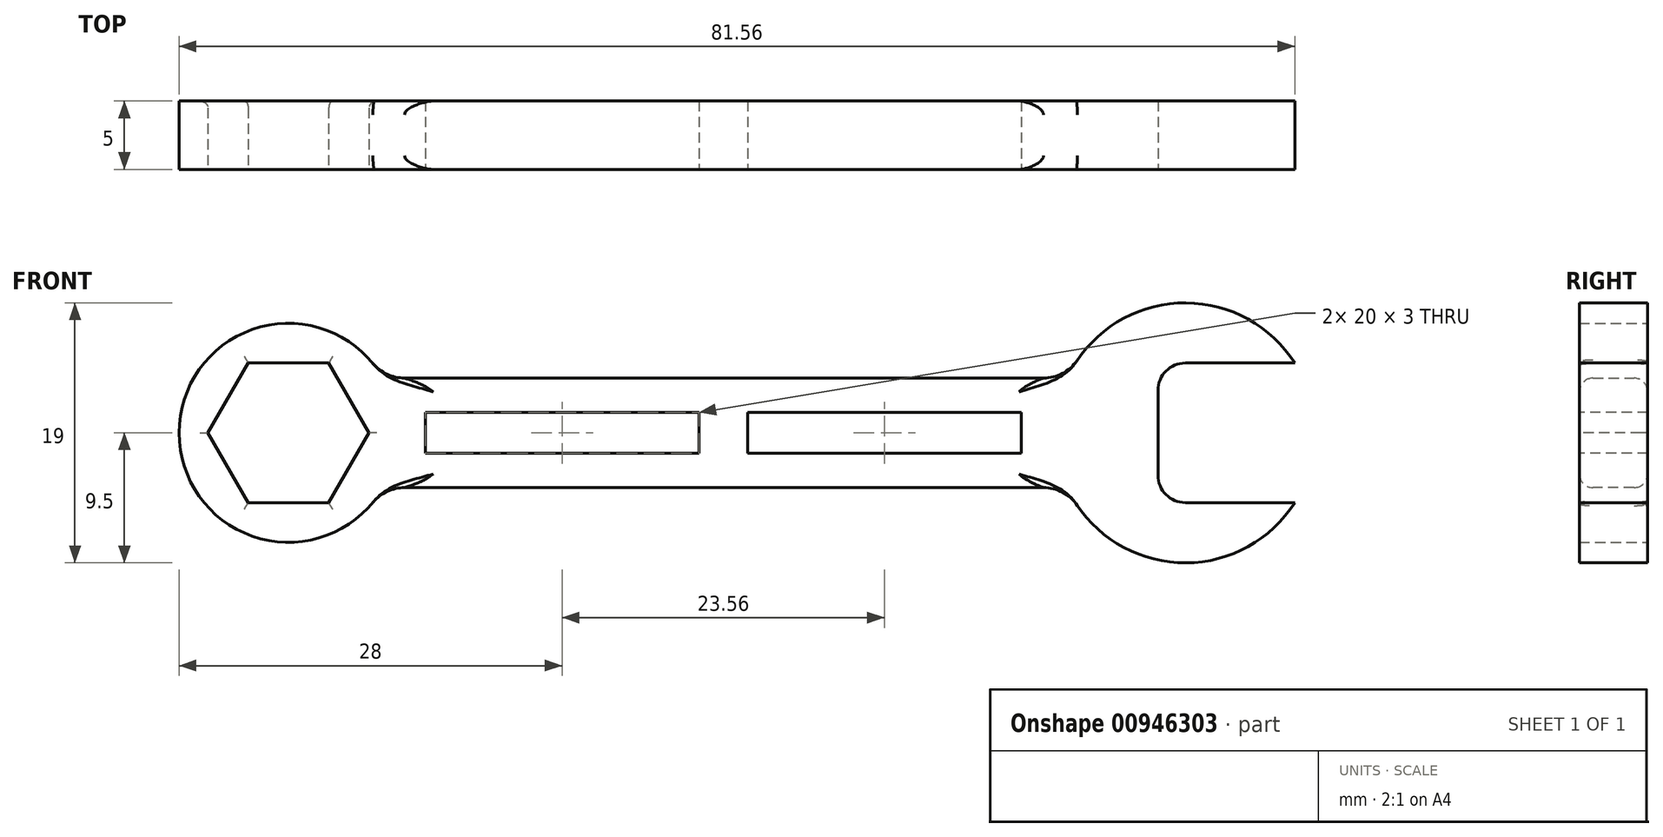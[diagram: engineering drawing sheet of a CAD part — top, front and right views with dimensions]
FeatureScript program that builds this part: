
annotation { "Feature Type Name" : "Feature", "Feature Type Description" : "" }
export const myFeature = defineFeature(function(context is Context, id is Id, definition is map)
    precondition{}
    {
        {
            var Q0;
            Q0=qCreatedBy(makeId("Front.planeOp"),FACE);
            var sketch = newSketch(context, id + "F0", { "sketchPlane" : qUnion([Q0])});
            skCircle(sketch, "E0", {"center": v(0, 0) * mm, "radius": 8 * mm});
            skLineSegment(sketch, "E1.bottom", {"start": v(6.93, 4) * mm, "end": v(56.93, 4) * mm});
            skLineSegment(sketch, "E1.top", {"start": v(6.93, -4) * mm, "end": v(56.93, -4) * mm});
            skLineSegment(sketch, "E1.left", {"start": v(6.93, 4) * mm, "end": v(6.93, -4) * mm});
            skLineSegment(sketch, "E1.right", {"start": v(56.93, 4) * mm, "end": v(56.93, -4) * mm});
            skCircle(sketch, "E2", {"center": v(65.55, 0) * mm, "radius": 9.5 * mm});
            skSolve(sketch);
        }
        {
            var Q0;
            {var subQ0=sQuery(id+"F0.wireOp",EDGE,"E1.left");Q0=makeQuery(id+"F0.imprint","IMPRINT",FACE,{"disambiguationData":[TD([[makeQuery(id+"F0.imprint","IMPRINT",EDGE,{"derivedFrom":subQ0}),-1.0]])]});}
            var Q1;
            {var subQ0=sQuery(id+"F0.wireOp",EDGE,"E1.left");Q1=makeQuery(id+"F0.imprint","IMPRINT",FACE,{"disambiguationData":[TD([[makeQuery(id+"F0.imprint","IMPRINT",EDGE,{"derivedFrom":subQ0}),1.0]])]});}
            var Q2;
            {var subQ1=sQuery(id+"F0.wireOp",EDGE,"E1.bottom");Q2=makeQuery(id+"F0.imprint","IMPRINT",FACE,{"disambiguationData":[TD([[makeQuery(id+"F0.imprint","IMPRINT",EDGE,{"derivedFrom":subQ1}),-1.0]])]});}
            var Q3;
            {var subQ0=sQuery(id+"F0.wireOp",EDGE,"E1.right");Q3=makeQuery(id+"F0.imprint","IMPRINT",FACE,{"disambiguationData":[TD([[makeQuery(id+"F0.imprint","IMPRINT",EDGE,{"derivedFrom":subQ0}),-1.0]])]});}
            var Q4;
            {var subQ0=sQuery(id+"F0.wireOp",EDGE,"E1.right");Q4=makeQuery(id+"F0.imprint","IMPRINT",FACE,{"disambiguationData":[TD([[makeQuery(id+"F0.imprint","IMPRINT",EDGE,{"derivedFrom":subQ0}),1.0]])]});}
            extrude(context, id + "F1", {"entities" : qUnion([Q0, Q1, Q2, Q3, Q4]), "depth" : 5 * mm, "offsetDistance" : 25 * mm});
        }
        {
            var Q0;
            Q0=makeQuery(id+"F1.opExtrude","CAP_FACE",FACE,{"disambiguationData":[OSD([sQuery(id+"F0.wireOp",EDGE,"E0"),sQuery(id+"F0.wireOp",EDGE,"E1.bottom"),sQuery(id+"F0.wireOp",EDGE,"E1.top"),sQuery(id+"F0.wireOp",EDGE,"E2")])],"isStart":false});
            var sketch = newSketch(context, id + "F2", { "sketchPlane" : qUnion([Q0])});
            skCircle(sketch, "E3.cCircle", {"center": v(0, 0) * mm, "radius": 5.1 * mm, "construction": true});
            skLineSegment(sketch, "E3.0", {"start": v(-2.94, 5.1) * mm, "end": v(2.94, 5.1) * mm});
            skLineSegment(sketch, "E3.1", {"start": v(2.94, 5.1) * mm, "end": v(5.89, 0) * mm});
            skLineSegment(sketch, "E3.2", {"start": v(5.89, 0) * mm, "end": v(2.94, -5.1) * mm});
            skLineSegment(sketch, "E3.3", {"start": v(2.94, -5.1) * mm, "end": v(-2.94, -5.1) * mm});
            skLineSegment(sketch, "E3.4", {"start": v(-2.94, -5.1) * mm, "end": v(-5.89, 0) * mm});
            skLineSegment(sketch, "E3.5", {"start": v(-5.89, 0) * mm, "end": v(-2.94, 5.1) * mm});
            skPoint(sketch, "E3.0.midPoint", {"position": v(0, 5.1) * mm});
            skSolve(sketch);
        }
        {
            var Q0;
            Q0=makeQuery(id+"F2.imprint","IMPRINT",FACE,{"disambiguationData":[TD([[makeQuery(id+"F2.imprint","IMPRINT",EDGE,{"derivedFrom":sQuery(id+"F2.wireOp",EDGE,"E3.0")}),-1.0]])]});
            extrude(context, id + "F3", {"entities" : qUnion([Q0]), "operationType" : NewBodyOperationType.REMOVE, "endBound" : BoundingType.THROUGH_ALL, "oppositeDirection" : true, "depth" : 25 * mm, "offsetDistance" : 25 * mm});
        }
        {
            var Q0;
            Q0=makeQuery(id+"F1.opExtrude","CAP_FACE",FACE,{"disambiguationData":[OSD([sQuery(id+"F0.wireOp",EDGE,"E0"),sQuery(id+"F0.wireOp",EDGE,"E1.bottom"),sQuery(id+"F0.wireOp",EDGE,"E1.top"),sQuery(id+"F0.wireOp",EDGE,"E2")])],"isStart":false});
            var sketch = newSketch(context, id + "F4", { "sketchPlane" : qUnion([Q0])});
            skLineSegment(sketch, "E4.bottom", {"start": v(63.56, 5.1) * mm, "end": v(73.56, 5.1) * mm});
            skLineSegment(sketch, "E4.top", {"start": v(63.56, -5.1) * mm, "end": v(73.56, -5.1) * mm});
            skLineSegment(sketch, "E4.left", {"start": v(63.56, 5.1) * mm, "end": v(63.56, -5.1) * mm});
            skLineSegment(sketch, "E4.right", {"start": v(73.56, 5.1) * mm, "end": v(73.56, -5.1) * mm});
            skLineSegment(sketch, "E5", {"start": v(0, 0) * mm, "end": v(77.1, 0) * mm, "construction": true});
            skSolve(sketch);
        }
        {
            var Q0;
            Q0=makeQuery(id+"F4.imprint","IMPRINT",FACE,{"disambiguationData":[TD([[makeQuery(id+"F4.imprint","IMPRINT",EDGE,{"derivedFrom":sQuery(id+"F4.wireOp",EDGE,"E4.bottom")}),-1.0]])]});
            var Q1;
            {var subQ0=sQuery(id+"F4.wireOp",EDGE,"E4.right");Q1=makeQuery(id+"F4.imprint","IMPRINT",FACE,{"disambiguationData":[TD([[makeQuery(id+"F4.imprint","IMPRINT",EDGE,{"derivedFrom":subQ0}),1.0]])]});}
            extrude(context, id + "F5", {"entities" : qUnion([Q0, Q1]), "operationType" : NewBodyOperationType.REMOVE, "endBound" : BoundingType.THROUGH_ALL, "oppositeDirection" : true, "depth" : 25 * mm, "offsetDistance" : 25 * mm});
        }
        {
            var Q0;
            Q0=makeQuery(id+"F1.opExtrude","CAP_FACE",FACE,{"disambiguationData":[OSD([sQuery(id+"F0.wireOp",EDGE,"E0"),sQuery(id+"F0.wireOp",EDGE,"E1.bottom"),sQuery(id+"F0.wireOp",EDGE,"E1.top"),sQuery(id+"F0.wireOp",EDGE,"E2")])],"isStart":false});
            var sketch = newSketch(context, id + "F6", { "sketchPlane" : qUnion([Q0])});
            skLineSegment(sketch, "E6.bottom", {"start": v(10, 1.5) * mm, "end": v(53.56, 1.5) * mm});
            skLineSegment(sketch, "E6.top", {"start": v(10, -1.5) * mm, "end": v(53.56, -1.5) * mm});
            skLineSegment(sketch, "E6.left", {"start": v(10, 1.5) * mm, "end": v(10, -1.5) * mm});
            skLineSegment(sketch, "E6.right", {"start": v(53.56, 1.5) * mm, "end": v(53.56, -1.5) * mm});
            skLineSegment(sketch, "E7", {"start": v(30, 1.5) * mm, "end": v(30, -1.5) * mm});
            skLineSegment(sketch, "E8", {"start": v(33.56, 1.5) * mm, "end": v(33.56, -1.5) * mm});
            skSolve(sketch);
        }
        {
            var Q0;
            {var subQ0=sQuery(id+"F6.wireOp",EDGE,"E6.left");Q0=makeQuery(id+"F6.imprint","IMPRINT",FACE,{"disambiguationData":[TD([[makeQuery(id+"F6.imprint","IMPRINT",EDGE,{"derivedFrom":subQ0}),1.0]])]});}
            var Q1;
            {var subQ0=sQuery(id+"F6.wireOp",EDGE,"E6.right");Q1=makeQuery(id+"F6.imprint","IMPRINT",FACE,{"disambiguationData":[TD([[makeQuery(id+"F6.imprint","IMPRINT",EDGE,{"derivedFrom":subQ0}),-1.0]])]});}
            extrude(context, id + "F7", {"entities" : qUnion([Q0, Q1]), "operationType" : NewBodyOperationType.REMOVE, "endBound" : BoundingType.THROUGH_ALL, "oppositeDirection" : true, "depth" : 25 * mm, "offsetDistance" : 25 * mm});
        }
        {
            var Q0;
            Q0=makeQuery(id+"F3.boolean.opBoolean","COPY",EDGE,{"derivedFrom":makeQuery(id+"F3.opExtrude","CAP_EDGE",EDGE,{"disambiguationData":[OSD([sQuery(id+"F2.wireOp",EDGE,"E3.4")])],"isStart":true})});
            var Q1;
            Q1=makeQuery(id+"F3.boolean.opBoolean","COPY",EDGE,{"derivedFrom":makeQuery(id+"F3.opExtrude","CAP_EDGE",EDGE,{"disambiguationData":[OSD([sQuery(id+"F2.wireOp",EDGE,"E3.5")])],"isStart":true})});
            var Q2;
            Q2=makeQuery(id+"F3.boolean.opBoolean","COPY",EDGE,{"derivedFrom":makeQuery(id+"F3.opExtrude","CAP_EDGE",EDGE,{"disambiguationData":[OSD([sQuery(id+"F2.wireOp",EDGE,"E3.0")])],"isStart":true})});
            var Q3;
            Q3=makeQuery(id+"F3.boolean.opBoolean","COPY",EDGE,{"derivedFrom":makeQuery(id+"F3.opExtrude","CAP_EDGE",EDGE,{"disambiguationData":[OSD([sQuery(id+"F2.wireOp",EDGE,"E3.1")])],"isStart":true})});
            var Q4;
            Q4=makeQuery(id+"F3.boolean.opBoolean","COPY",EDGE,{"derivedFrom":makeQuery(id+"F3.opExtrude","CAP_EDGE",EDGE,{"disambiguationData":[OSD([sQuery(id+"F2.wireOp",EDGE,"E3.2")])],"isStart":true})});
            var Q5;
            Q5=makeQuery(id+"F3.boolean.opBoolean","COPY",EDGE,{"derivedFrom":makeQuery(id+"F3.opExtrude","CAP_EDGE",EDGE,{"disambiguationData":[OSD([sQuery(id+"F2.wireOp",EDGE,"E3.3")])],"isStart":true})});
            var Q6;
            Q6=makeQuery(id+"F3.boolean.opBoolean","INTERSECT",EDGE,{"derivedFrom":[makeQuery(id+"F1.opExtrude","CAP_FACE",FACE,{"disambiguationData":[OSD([sQuery(id+"F0.wireOp",EDGE,"E0"),sQuery(id+"F0.wireOp",EDGE,"E1.bottom"),sQuery(id+"F0.wireOp",EDGE,"E1.top"),sQuery(id+"F0.wireOp",EDGE,"E2")])],"isStart":true}),makeQuery(id+"F3.opExtrude","SWEPT_FACE",FACE,{"disambiguationData":[OSD([sQuery(id+"F2.wireOp",EDGE,"E3.0")])]})]});
            var Q7;
            Q7=makeQuery(id+"F3.boolean.opBoolean","INTERSECT",EDGE,{"derivedFrom":[makeQuery(id+"F1.opExtrude","CAP_FACE",FACE,{"disambiguationData":[OSD([sQuery(id+"F0.wireOp",EDGE,"E0"),sQuery(id+"F0.wireOp",EDGE,"E1.bottom"),sQuery(id+"F0.wireOp",EDGE,"E1.top"),sQuery(id+"F0.wireOp",EDGE,"E2")])],"isStart":true}),makeQuery(id+"F3.opExtrude","SWEPT_FACE",FACE,{"disambiguationData":[OSD([sQuery(id+"F2.wireOp",EDGE,"E3.5")])]})]});
            var Q8;
            Q8=makeQuery(id+"F3.boolean.opBoolean","INTERSECT",EDGE,{"derivedFrom":[makeQuery(id+"F1.opExtrude","CAP_FACE",FACE,{"disambiguationData":[OSD([sQuery(id+"F0.wireOp",EDGE,"E0"),sQuery(id+"F0.wireOp",EDGE,"E1.bottom"),sQuery(id+"F0.wireOp",EDGE,"E1.top"),sQuery(id+"F0.wireOp",EDGE,"E2")])],"isStart":true}),makeQuery(id+"F3.opExtrude","SWEPT_FACE",FACE,{"disambiguationData":[OSD([sQuery(id+"F2.wireOp",EDGE,"E3.4")])]})]});
            var Q9;
            Q9=makeQuery(id+"F3.boolean.opBoolean","INTERSECT",EDGE,{"derivedFrom":[makeQuery(id+"F1.opExtrude","CAP_FACE",FACE,{"disambiguationData":[OSD([sQuery(id+"F0.wireOp",EDGE,"E0"),sQuery(id+"F0.wireOp",EDGE,"E1.bottom"),sQuery(id+"F0.wireOp",EDGE,"E1.top"),sQuery(id+"F0.wireOp",EDGE,"E2")])],"isStart":true}),makeQuery(id+"F3.opExtrude","SWEPT_FACE",FACE,{"disambiguationData":[OSD([sQuery(id+"F2.wireOp",EDGE,"E3.3")])]})]});
            var Q10;
            Q10=makeQuery(id+"F3.boolean.opBoolean","INTERSECT",EDGE,{"derivedFrom":[makeQuery(id+"F1.opExtrude","CAP_FACE",FACE,{"disambiguationData":[OSD([sQuery(id+"F0.wireOp",EDGE,"E0"),sQuery(id+"F0.wireOp",EDGE,"E1.bottom"),sQuery(id+"F0.wireOp",EDGE,"E1.top"),sQuery(id+"F0.wireOp",EDGE,"E2")])],"isStart":true}),makeQuery(id+"F3.opExtrude","SWEPT_FACE",FACE,{"disambiguationData":[OSD([sQuery(id+"F2.wireOp",EDGE,"E3.2")])]})]});
            var Q11;
            Q11=makeQuery(id+"F3.boolean.opBoolean","INTERSECT",EDGE,{"derivedFrom":[makeQuery(id+"F1.opExtrude","CAP_FACE",FACE,{"disambiguationData":[OSD([sQuery(id+"F0.wireOp",EDGE,"E0"),sQuery(id+"F0.wireOp",EDGE,"E1.bottom"),sQuery(id+"F0.wireOp",EDGE,"E1.top"),sQuery(id+"F0.wireOp",EDGE,"E2")])],"isStart":true}),makeQuery(id+"F3.opExtrude","SWEPT_FACE",FACE,{"disambiguationData":[OSD([sQuery(id+"F2.wireOp",EDGE,"E3.1")])]})]});
            fillet(context, id + "F8", {"entities" : qUnion([Q0, Q1, Q2, Q3, Q4, Q5, Q6, Q7, Q8, Q9, Q10, Q11]), "radius" : .5 * mm, "tangentPropagation" : true, "allowEdgeOverflow" : false});
        }
        {
            var Q0;
            Q0=makeQuery(id+"F5.boolean.opBoolean","COPY",EDGE,{"derivedFrom":makeQuery(id+"F5.opExtrude","SWEPT_EDGE",EDGE,{"disambiguationData":[OSD([sQuery(id+"F4.wireOp",EDGE,"E4.bottom"),sQuery(id+"F4.wireOp",EDGE,"E4.left")])]})});
            var Q1;
            Q1=makeQuery(id+"F5.boolean.opBoolean","COPY",EDGE,{"derivedFrom":makeQuery(id+"F5.opExtrude","SWEPT_EDGE",EDGE,{"disambiguationData":[OSD([sQuery(id+"F4.wireOp",EDGE,"E4.top"),sQuery(id+"F4.wireOp",EDGE,"E4.left")])]})});
            fillet(context, id + "F9", {"entities" : qUnion([Q0, Q1]), "radius" : 2 * mm, "tangentPropagation" : true, "allowEdgeOverflow" : false});
        }
        {
            var Q0;
            Q0=makeQuery(id+"F1.opExtrude","CAP_EDGE",EDGE,{"disambiguationData":[OSD([sQuery(id+"F0.wireOp",EDGE,"E1.bottom")])],"isStart":false});
            var Q1;
            Q1=makeQuery(id+"F1.opExtrude","CAP_EDGE",EDGE,{"disambiguationData":[OSD([sQuery(id+"F0.wireOp",EDGE,"E1.bottom")])],"isStart":true});
            var Q2;
            Q2=makeQuery(id+"F1.opExtrude","CAP_EDGE",EDGE,{"disambiguationData":[OSD([sQuery(id+"F0.wireOp",EDGE,"E1.top")])],"isStart":true});
            var Q3;
            Q3=makeQuery(id+"F1.opExtrude","CAP_EDGE",EDGE,{"disambiguationData":[OSD([sQuery(id+"F0.wireOp",EDGE,"E1.top")])],"isStart":false});
            fillet(context, id + "F10", {"entities" : qUnion([Q0, Q1, Q2, Q3]), "radius" : 1 * mm, "tangentPropagation" : true, "allowEdgeOverflow" : false});
        }
        {
            var Q0;
            Q0=makeQuery(id+"F1.opExtrude","SWEPT_EDGE",EDGE,{"disambiguationData":[OSD([sQuery(id+"F0.wireOp",EDGE,"E1.top"),sQuery(id+"F0.wireOp",EDGE,"E1.right"),sQuery(id+"F0.wireOp",EDGE,"E2")])]});
            var Q1;
            Q1=makeQuery(id+"F1.opExtrude","SWEPT_EDGE",EDGE,{"disambiguationData":[OSD([sQuery(id+"F0.wireOp",EDGE,"E1.bottom"),sQuery(id+"F0.wireOp",EDGE,"E1.right"),sQuery(id+"F0.wireOp",EDGE,"E2")])]});
            var Q2;
            Q2=makeQuery(id+"F1.opExtrude","SWEPT_EDGE",EDGE,{"disambiguationData":[OSD([sQuery(id+"F0.wireOp",EDGE,"E0"),sQuery(id+"F0.wireOp",EDGE,"E1.top"),sQuery(id+"F0.wireOp",EDGE,"E1.left")])]});
            var Q3;
            Q3=makeQuery(id+"F1.opExtrude","SWEPT_EDGE",EDGE,{"disambiguationData":[OSD([sQuery(id+"F0.wireOp",EDGE,"E0"),sQuery(id+"F0.wireOp",EDGE,"E1.bottom"),sQuery(id+"F0.wireOp",EDGE,"E1.left")])]});
            fillet(context, id + "F11", {"entities" : qUnion([Q0, Q1, Q2, Q3]), "radius" : 3 * mm, "tangentPropagation" : true, "allowEdgeOverflow" : false});
        }
    });
